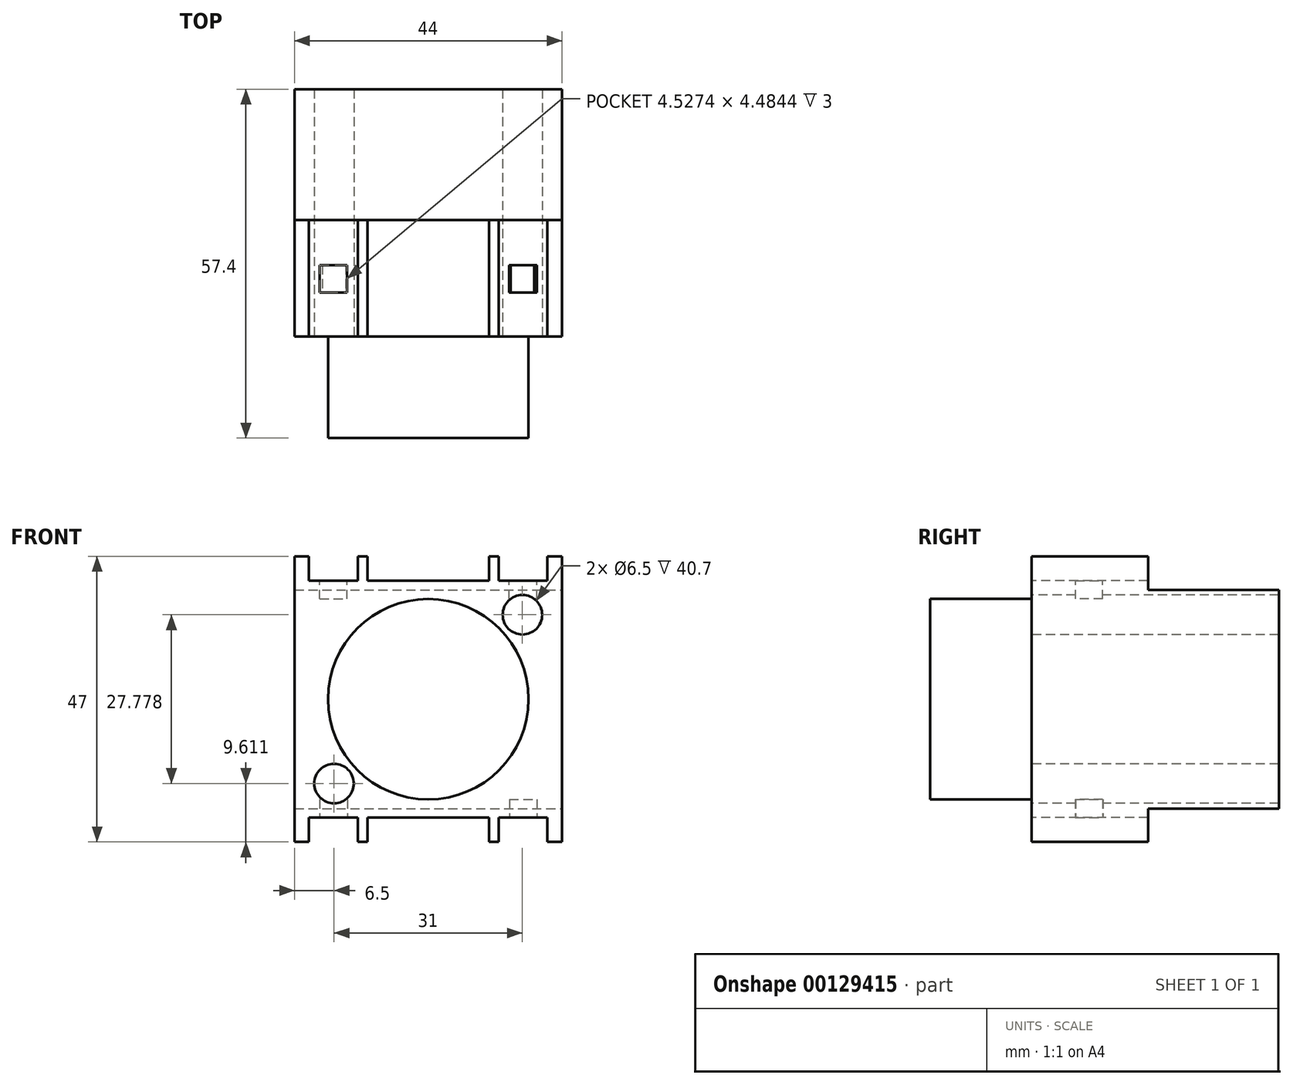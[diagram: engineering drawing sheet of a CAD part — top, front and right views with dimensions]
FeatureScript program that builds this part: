
annotation { "Feature Type Name" : "Feature", "Feature Type Description" : "" }
export const myFeature = defineFeature(function(context is Context, id is Id, definition is map)
    precondition{}
    {
        {
            var Q0;
            Q0=qCreatedBy(makeId("Front.planeOp"),FACE);
            var sketch = newSketch(context, id + "F0", { "sketchPlane" : qUnion([Q0])});
            skLineSegment(sketch, "E0.bottom", {"start": v(22, -23.5) * mm, "end": v(19.62, -23.5) * mm});
            skLineSegment(sketch, "E0.left", {"start": v(22, -23.5) * mm, "end": v(22, 23.5) * mm});
            skLineSegment(sketch, "E0.right", {"start": v(-22, -23.5) * mm, "end": v(-22, 23.5) * mm});
            skPoint(sketch, "E0.middle", {"position": v(0, 0) * mm});
            skLineSegment(sketch, "E1", {"start": v(-22, 23.5) * mm, "end": v(-22, 19.5) * mm});
            skLineSegment(sketch, "E2", {"start": v(-19.62, 19.5) * mm, "end": v(-11.58, 19.5) * mm});
            skLineSegment(sketch, "E3.MirrorCS", {"start": v(-19.62, -19.5) * mm, "end": v(-11.58, -19.5) * mm});
            skLineSegment(sketch, "E4.left", {"start": v(2.3, 19.5) * mm, "end": v(2.3, 23.5) * mm});
            skLineSegment(sketch, "E4.right", {"start": v(-2.3, 19.5) * mm, "end": v(-2.3, 23.5) * mm});
            skLineSegment(sketch, "E5", {"start": v(-2.3, 19.5) * mm, "end": v(-9.98, 19.5) * mm});
            skLineSegment(sketch, "E6.left", {"start": v(-9.98, 19.5) * mm, "end": v(-9.98, 23.5) * mm});
            skLineSegment(sketch, "E6.right", {"start": v(-11.58, 19.5) * mm, "end": v(-11.58, 23.5) * mm});
            skLineSegment(sketch, "E7.top", {"start": v(-22, 23.5) * mm, "end": v(-19.62, 23.5) * mm});
            skLineSegment(sketch, "E7.left", {"start": v(-22, 19.5) * mm, "end": v(-22, 23.5) * mm});
            skLineSegment(sketch, "E7.right", {"start": v(-19.62, 19.5) * mm, "end": v(-19.62, 23.5) * mm});
            skLineSegment(sketch, "E8.MirrorCS", {"start": v(22, 23.5) * mm, "end": v(19.62, 23.5) * mm});
            skLineSegment(sketch, "E9.MirrorCS", {"start": v(22, 23.5) * mm, "end": v(22, 19.5) * mm});
            skLineSegment(sketch, "E10.MirrorCS", {"start": v(22, 19.5) * mm, "end": v(22, 23.5) * mm});
            skLineSegment(sketch, "E11.MirrorCS", {"start": v(9.98, 19.5) * mm, "end": v(9.98, 23.5) * mm});
            skLineSegment(sketch, "E12.MirrorCS", {"start": v(11.58, 19.5) * mm, "end": v(11.58, 23.5) * mm});
            skLineSegment(sketch, "E13.MirrorCS", {"start": v(19.62, 19.5) * mm, "end": v(19.62, 23.5) * mm});
            skLineSegment(sketch, "E14.MirrorCS", {"start": v(-22, -23.5) * mm, "end": v(-19.62, -23.5) * mm});
            skLineSegment(sketch, "E15.MirrorCS", {"start": v(9.98, -19.5) * mm, "end": v(9.98, -23.5) * mm});
            skLineSegment(sketch, "E16.MirrorCS", {"start": v(-9.98, -19.5) * mm, "end": v(-9.98, -23.5) * mm});
            skLineSegment(sketch, "E17.MirrorCS", {"start": v(-2.3, -19.5) * mm, "end": v(-2.3, -23.5) * mm});
            skLineSegment(sketch, "E18.MirrorCS", {"start": v(-11.58, -19.5) * mm, "end": v(-11.58, -23.5) * mm});
            skLineSegment(sketch, "E19.MirrorCS", {"start": v(11.58, -19.5) * mm, "end": v(11.58, -23.5) * mm});
            skLineSegment(sketch, "E20.MirrorCS", {"start": v(22, -23.5) * mm, "end": v(22, -19.5) * mm});
            skLineSegment(sketch, "E21.MirrorCS", {"start": v(-22, -23.5) * mm, "end": v(-22, -19.5) * mm});
            skPoint(sketch, "E22.MirrorP", {"position": v(10.78, -23.5) * mm});
            skLineSegment(sketch, "E23.MirrorCS", {"start": v(-22, -19.5) * mm, "end": v(-22, -23.5) * mm});
            skLineSegment(sketch, "E24.MirrorCS", {"start": v(22, -19.5) * mm, "end": v(22, -23.5) * mm});
            skLineSegment(sketch, "E25.MirrorCS", {"start": v(19.62, -19.5) * mm, "end": v(19.62, -23.5) * mm});
            skPoint(sketch, "E26.MirrorP", {"position": v(0, -23.5) * mm});
            skLineSegment(sketch, "E27.MirrorCS", {"start": v(2.3, -19.5) * mm, "end": v(2.3, -23.5) * mm});
            skLineSegment(sketch, "E28.MirrorCS", {"start": v(-19.62, -19.5) * mm, "end": v(-19.62, -23.5) * mm});
            skPoint(sketch, "E29.MirrorP", {"position": v(-10.78, -23.5) * mm});
            skLineSegment(sketch, "E30.trimOffspring", {"start": v(-19.62, -23.5) * mm, "end": v(-22, -23.5) * mm});
            skLineSegment(sketch, "E31.trimOffspring", {"start": v(-9.98, -23.5) * mm, "end": v(-11.58, -23.5) * mm});
            skLineSegment(sketch, "E32.trimOffspring", {"start": v(2.3, -23.5) * mm, "end": v(-2.3, -23.5) * mm});
            skLineSegment(sketch, "E33.trimOffspring", {"start": v(11.58, -23.5) * mm, "end": v(9.98, -23.5) * mm});
            skLineSegment(sketch, "E34.trimOffspring", {"start": v(11.58, 23.5) * mm, "end": v(9.98, 23.5) * mm});
            skLineSegment(sketch, "E35.trimOffspring", {"start": v(-9.98, 23.5) * mm, "end": v(-11.58, 23.5) * mm});
            skLineSegment(sketch, "E36.trimOffspring", {"start": v(11.58, 19.5) * mm, "end": v(19.62, 19.5) * mm});
            skLineSegment(sketch, "E37.trimOffspring", {"start": v(2.3, 19.5) * mm, "end": v(9.98, 19.5) * mm});
            skLineSegment(sketch, "E38", {"start": v(-2.3, 23.5) * mm, "end": v(2.3, 23.5) * mm});
            skLineSegment(sketch, "E39.trimOffspring", {"start": v(-9.98, 19.5) * mm, "end": v(-2.3, 19.5) * mm});
            skLineSegment(sketch, "E40.trimOffspring", {"start": v(-19.62, 23.5) * mm, "end": v(-22, 23.5) * mm});
            skLineSegment(sketch, "E41.trimOffspring", {"start": v(11.58, -19.5) * mm, "end": v(19.62, -19.5) * mm});
            skLineSegment(sketch, "E42.trimOffspring", {"start": v(2.3, -19.5) * mm, "end": v(9.98, -19.5) * mm});
            skLineSegment(sketch, "E43.trimOffspring", {"start": v(-9.98, -19.5) * mm, "end": v(-2.3, -19.5) * mm});
            skCircle(sketch, "E44", {"center": v(0, 0) * mm, "radius": 16.5 * mm});
            skLineSegment(sketch, "E45", {"start": v(-22, 23.5) * mm, "end": v(-22, 13.9) * mm});
            skLineSegment(sketch, "E46", {"start": v(-22, 13.9) * mm, "end": v(-15.5, 13.89) * mm});
            skCircle(sketch, "E47", {"center": v(-15.5, 13.89) * mm, "radius": 3.25 * mm});
            skCircle(sketch, "E48.MirrorC", {"center": v(15.5, 13.89) * mm, "radius": 3.25 * mm});
            skCircle(sketch, "E49.MirrorC", {"center": v(15.5, -13.89) * mm, "radius": 3.25 * mm});
            skCircle(sketch, "E50.MirrorC", {"center": v(-15.5, -13.89) * mm, "radius": 3.25 * mm});
            skSolve(sketch);
        }
        {
            var Q0;
            Q0=makeQuery(id+"F0.imprint","IMPRINT",FACE,{"disambiguationData":[TD([[makeQuery(id+"F0.imprint","IMPRINT",EDGE,{"derivedFrom":sQuery(id+"F0.wireOp",EDGE,"E0.left")}),1.0]])]});
            var Q1;
            Q1=makeQuery(id+"F0.imprint","IMPRINT",FACE,{"disambiguationData":[TD([[makeQuery(id+"F0.imprint","IMPRINT",EDGE,{"derivedFrom":sQuery(id+"F0.wireOp",EDGE,"E47")}),1.0]])]});
            var Q2;
            Q2=makeQuery(id+"F0.imprint","IMPRINT",FACE,{"disambiguationData":[TD([[makeQuery(id+"F0.imprint","IMPRINT",EDGE,{"derivedFrom":sQuery(id+"F0.wireOp",EDGE,"E48.MirrorC")}),-1.0]])]});
            var Q3;
            Q3=makeQuery(id+"F0.imprint","IMPRINT",FACE,{"disambiguationData":[TD([[makeQuery(id+"F0.imprint","IMPRINT",EDGE,{"derivedFrom":sQuery(id+"F0.wireOp",EDGE,"E44")}),1.0]])]});
            var Q4;
            Q4=makeQuery(id+"F0.imprint","IMPRINT",FACE,{"disambiguationData":[TD([[makeQuery(id+"F0.imprint","IMPRINT",EDGE,{"derivedFrom":sQuery(id+"F0.wireOp",EDGE,"E50.MirrorC")}),-1.0]])]});
            var Q5;
            Q5=makeQuery(id+"F0.imprint","IMPRINT",FACE,{"disambiguationData":[TD([[makeQuery(id+"F0.imprint","IMPRINT",EDGE,{"derivedFrom":sQuery(id+"F0.wireOp",EDGE,"E49.MirrorC")}),1.0]])]});
            extrude(context, id + "F1", {"entities" : qUnion([Q0, Q1, Q2, Q3, Q4, Q5]), "oppositeDirection" : true, "depth" : 22.2 * mm});
        }
        {
            var Q0;
            Q0=makeQuery(id+"F1.opExtrude","SWEPT_FACE",FACE,{"disambiguationData":[OSD([sQuery(id+"F0.wireOp",EDGE,"E38")])]});
            var sketch = newSketch(context, id + "F2", { "sketchPlane" : qUnion([Q0])});
            skLineSegment(sketch, "E51.bottom", {"start": v(-2.3, 22.2) * mm, "end": v(2.3, 22.2) * mm});
            skLineSegment(sketch, "E51.top", {"start": v(-2.3, 1.7) * mm, "end": v(2.3, 1.7) * mm});
            skLineSegment(sketch, "E51.left", {"start": v(-2.3, 22.2) * mm, "end": v(-2.3, 1.7) * mm});
            skLineSegment(sketch, "E51.right", {"start": v(2.3, 22.2) * mm, "end": v(2.3, 1.7) * mm});
            skSolve(sketch);
        }
        {
            var Q0;
            Q0=makeQuery(id+"F2.imprint","IMPRINT",FACE,{"disambiguationData":[TD([[makeQuery(id+"F2.imprint","IMPRINT",EDGE,{"derivedFrom":sQuery(id+"F2.wireOp",EDGE,"E51.bottom")}),-1.0]])]});
            extrude(context, id + "F3", {"entities" : qUnion([Q0]), "operationType" : NewBodyOperationType.REMOVE, "oppositeDirection" : true, "depth" : 4 * mm});
        }
        {
            var Q0;
            Q0=makeQuery(id+"F1.opExtrude","SWEPT_FACE",FACE,{"disambiguationData":[OSD([sQuery(id+"F0.wireOp",EDGE,"E32.trimOffspring")])]});
            var sketch = newSketch(context, id + "F4", { "sketchPlane" : qUnion([Q0])});
            skLineSegment(sketch, "E52.bottom", {"start": v(2.3, -22.2) * mm, "end": v(-2.3, -22.2) * mm});
            skLineSegment(sketch, "E52.top", {"start": v(2.3, -1.7) * mm, "end": v(-2.3, -1.7) * mm});
            skLineSegment(sketch, "E52.left", {"start": v(2.3, -22.2) * mm, "end": v(2.3, -1.7) * mm});
            skLineSegment(sketch, "E52.right", {"start": v(-2.3, -22.2) * mm, "end": v(-2.3, -1.7) * mm});
            skSolve(sketch);
        }
        {
            var Q0;
            Q0=makeQuery(id+"F4.imprint","IMPRINT",FACE,{"disambiguationData":[TD([[makeQuery(id+"F4.imprint","IMPRINT",EDGE,{"derivedFrom":sQuery(id+"F4.wireOp",EDGE,"E52.bottom")}),-1.0]])]});
            extrude(context, id + "F5", {"entities" : qUnion([Q0]), "operationType" : NewBodyOperationType.REMOVE, "oppositeDirection" : true, "depth" : 4 * mm});
        }
        {
            var Q0;
            Q0=makeQuery(id+"F0.imprint","IMPRINT",FACE,{"disambiguationData":[TD([[makeQuery(id+"F0.imprint","IMPRINT",EDGE,{"derivedFrom":sQuery(id+"F0.wireOp",EDGE,"E47")}),1.0]])]});
            var Q1;
            Q1=makeQuery(id+"F0.imprint","IMPRINT",FACE,{"disambiguationData":[TD([[makeQuery(id+"F0.imprint","IMPRINT",EDGE,{"derivedFrom":sQuery(id+"F0.wireOp",EDGE,"E48.MirrorC")}),-1.0]])]});
            var Q2;
            Q2=makeQuery(id+"F0.imprint","IMPRINT",FACE,{"disambiguationData":[TD([[makeQuery(id+"F0.imprint","IMPRINT",EDGE,{"derivedFrom":sQuery(id+"F0.wireOp",EDGE,"E49.MirrorC")}),1.0]])]});
            var Q3;
            Q3=makeQuery(id+"F0.imprint","IMPRINT",FACE,{"disambiguationData":[TD([[makeQuery(id+"F0.imprint","IMPRINT",EDGE,{"derivedFrom":sQuery(id+"F0.wireOp",EDGE,"E50.MirrorC")}),-1.0]])]});
            extrude(context, id + "F6", {"entities" : qUnion([Q0, Q1, Q2, Q3]), "operationType" : NewBodyOperationType.REMOVE, "oppositeDirection" : true, "depth" : 3 * mm});
        }
        {
            var Q0;
            Q0=makeQuery(id+"F0.imprint","IMPRINT",FACE,{"disambiguationData":[TD([[makeQuery(id+"F0.imprint","IMPRINT",EDGE,{"derivedFrom":sQuery(id+"F0.wireOp",EDGE,"E44")}),1.0]])]});
            extrude(context, id + "F7", {"entities" : qUnion([Q0]), "operationType" : NewBodyOperationType.ADD, "depth" : 13.7 * mm});
        }
        {
            var Q0;
            Q0=makeQuery(id+"F1.opExtrude","CAP_FACE",FACE,{"disambiguationData":[OSD([sQuery(id+"F0.wireOp",EDGE,"E0.left"),sQuery(id+"F0.wireOp",EDGE,"E0.right"),sQuery(id+"F0.wireOp",EDGE,"E2"),sQuery(id+"F0.wireOp",EDGE,"E3.MirrorCS"),sQuery(id+"F0.wireOp",EDGE,"E4.left"),sQuery(id+"F0.wireOp",EDGE,"E4.right"),sQuery(id+"F0.wireOp",EDGE,"E6.left"),sQuery(id+"F0.wireOp",EDGE,"E6.right"),sQuery(id+"F0.wireOp",EDGE,"E7.right"),sQuery(id+"F0.wireOp",EDGE,"E8.MirrorCS"),sQuery(id+"F0.wireOp",EDGE,"E10.MirrorCS"),sQuery(id+"F0.wireOp",EDGE,"E11.MirrorCS"),sQuery(id+"F0.wireOp",EDGE,"E12.MirrorCS"),sQuery(id+"F0.wireOp",EDGE,"E13.MirrorCS"),sQuery(id+"F0.wireOp",EDGE,"E15.MirrorCS"),sQuery(id+"F0.wireOp",EDGE,"E16.MirrorCS"),sQuery(id+"F0.wireOp",EDGE,"E17.MirrorCS"),sQuery(id+"F0.wireOp",EDGE,"E18.MirrorCS"),sQuery(id+"F0.wireOp",EDGE,"E19.MirrorCS"),sQuery(id+"F0.wireOp",EDGE,"E23.MirrorCS"),sQuery(id+"F0.wireOp",EDGE,"E24.MirrorCS"),sQuery(id+"F0.wireOp",EDGE,"E25.MirrorCS"),sQuery(id+"F0.wireOp",EDGE,"E27.MirrorCS"),sQuery(id+"F0.wireOp",EDGE,"E28.MirrorCS"),sQuery(id+"F0.wireOp",EDGE,"E0.bottom"),sQuery(id+"F0.wireOp",EDGE,"E31.trimOffspring"),sQuery(id+"F0.wireOp",EDGE,"E32.trimOffspring"),sQuery(id+"F0.wireOp",EDGE,"E33.trimOffspring"),sQuery(id+"F0.wireOp",EDGE,"E34.trimOffspring"),sQuery(id+"F0.wireOp",EDGE,"E35.trimOffspring"),sQuery(id+"F0.wireOp",EDGE,"E36.trimOffspring"),sQuery(id+"F0.wireOp",EDGE,"E37.trimOffspring"),sQuery(id+"F0.wireOp",EDGE,"E38"),sQuery(id+"F0.wireOp",EDGE,"E39.trimOffspring"),sQuery(id+"F0.wireOp",EDGE,"E40.trimOffspring"),sQuery(id+"F0.wireOp",EDGE,"E42.trimOffspring"),sQuery(id+"F0.wireOp",EDGE,"E41.trimOffspring"),sQuery(id+"F0.wireOp",EDGE,"E30.trimOffspring"),sQuery(id+"F0.wireOp",EDGE,"E43.trimOffspring"),sQuery(id+"F0.wireOp",EDGE,"E45")])],"isStart":false});
            var sketch = newSketch(context, id + "F8", { "sketchPlane" : qUnion([Q0])});
            skPoint(sketch, "E53", {"position": v(0, 0) * mm});
            skLineSegment(sketch, "E54.bottom", {"start": v(22, 18) * mm, "end": v(-22, 18) * mm});
            skLineSegment(sketch, "E54.top", {"start": v(22, -18) * mm, "end": v(-22, -18) * mm});
            skLineSegment(sketch, "E54.left", {"start": v(22, 18) * mm, "end": v(22, -18) * mm});
            skLineSegment(sketch, "E54.right", {"start": v(-22, 18) * mm, "end": v(-22, -18) * mm});
            skSolve(sketch);
        }
        {
            var Q0;
            Q0=makeQuery(id+"F8.imprint","IMPRINT",FACE,{"disambiguationData":[TD([[makeQuery(id+"F8.imprint","IMPRINT",EDGE,{"derivedFrom":sQuery(id+"F8.wireOp",EDGE,"E54.bottom")}),1.0]])]});
            extrude(context, id + "F9", {"entities" : qUnion([Q0]), "operationType" : NewBodyOperationType.ADD, "depth" : 21.5 * mm});
        }
        {
            var Q0;
            Q0=makeQuery(id+"F1.opExtrude","SWEPT_FACE",FACE,{"disambiguationData":[OSD([sQuery(id+"F0.wireOp",EDGE,"E36.trimOffspring")])]});
            var sketch = newSketch(context, id + "F10", { "sketchPlane" : qUnion([Q0])});
            skLineSegment(sketch, "E55", {"start": v(15.6, 0) * mm, "end": v(15.6, 12.5) * mm});
            skLineSegment(sketch, "E56.bottom", {"start": v(17.86, 10.26) * mm, "end": v(13.34, 10.26) * mm});
            skLineSegment(sketch, "E56.top", {"start": v(17.86, 14.74) * mm, "end": v(13.34, 14.74) * mm});
            skLineSegment(sketch, "E56.left", {"start": v(17.86, 10.26) * mm, "end": v(17.86, 14.74) * mm});
            skLineSegment(sketch, "E56.right", {"start": v(13.34, 10.26) * mm, "end": v(13.34, 14.74) * mm});
            skPoint(sketch, "E56.middle", {"position": v(15.6, 12.5) * mm});
            skLineSegment(sketch, "E57.MirrorCS", {"start": v(-13.34, 10.26) * mm, "end": v(-13.34, 14.74) * mm});
            skLineSegment(sketch, "E58.MirrorCS", {"start": v(-17.86, 10.26) * mm, "end": v(-17.86, 14.74) * mm});
            skLineSegment(sketch, "E59.MirrorCS", {"start": v(-17.86, 14.74) * mm, "end": v(-13.34, 14.74) * mm});
            skPoint(sketch, "E60.MirrorP", {"position": v(-15.6, 12.5) * mm});
            skLineSegment(sketch, "E61.MirrorCS", {"start": v(-17.86, 10.26) * mm, "end": v(-13.34, 10.26) * mm});
            skSolve(sketch);
        }
        {
            var Q0;
            Q0=makeQuery(id+"F1.opExtrude","SWEPT_FACE",FACE,{"disambiguationData":[OSD([sQuery(id+"F0.wireOp",EDGE,"E3.MirrorCS")])]});
            var sketch = newSketch(context, id + "F11", { "sketchPlane" : qUnion([Q0])});
            skLineSegment(sketch, "E62.bottom", {"start": v(-13.32, -10.26) * mm, "end": v(-17.84, -10.26) * mm});
            skLineSegment(sketch, "E62.top", {"start": v(-13.32, -14.74) * mm, "end": v(-17.84, -14.74) * mm});
            skLineSegment(sketch, "E62.left", {"start": v(-13.32, -10.26) * mm, "end": v(-13.32, -14.74) * mm});
            skLineSegment(sketch, "E62.right", {"start": v(-17.84, -10.26) * mm, "end": v(-17.84, -14.74) * mm});
            skPoint(sketch, "E62.middle", {"position": v(-15.58, -12.5) * mm});
            skLineSegment(sketch, "E63.bottom", {"start": v(13.37, -10.2) * mm, "end": v(17.88, -10.2) * mm});
            skLineSegment(sketch, "E63.top", {"start": v(13.37, -14.8) * mm, "end": v(17.88, -14.8) * mm});
            skLineSegment(sketch, "E63.left", {"start": v(13.37, -10.2) * mm, "end": v(13.37, -14.8) * mm});
            skLineSegment(sketch, "E63.right", {"start": v(17.88, -10.2) * mm, "end": v(17.88, -14.8) * mm});
            skPoint(sketch, "E63.middle", {"position": v(15.63, -12.5) * mm});
            skPoint(sketch, "E63.middle.positionSnap0", {"position": v(-13.32, -12.5) * mm});
            skPoint(sketch, "E63.centerSnap0", {"position": v(-13.32, -12.5) * mm});
            skSolve(sketch);
        }
        {
            var Q0;
            Q0=makeQuery(id+"F10.imprint","IMPRINT",FACE,{"disambiguationData":[TD([[makeQuery(id+"F10.imprint","IMPRINT",EDGE,{"derivedFrom":sQuery(id+"F10.wireOp",EDGE,"E57.MirrorCS")}),1.0]])]});
            var Q1;
            Q1=makeQuery(id+"F10.imprint","IMPRINT",FACE,{"disambiguationData":[TD([[makeQuery(id+"F10.imprint","IMPRINT",EDGE,{"derivedFrom":sQuery(id+"F10.wireOp",EDGE,"E56.top")}),1.0]])]});
            extrude(context, id + "F12", {"entities" : qUnion([Q0, Q1]), "operationType" : NewBodyOperationType.REMOVE, "oppositeDirection" : true, "depth" : 3 * mm});
        }
        {
            var Q0;
            Q0=makeQuery(id+"F11.imprint","IMPRINT",FACE,{"disambiguationData":[TD([[makeQuery(id+"F11.imprint","IMPRINT",EDGE,{"derivedFrom":sQuery(id+"F11.wireOp",EDGE,"E63.bottom")}),-1.0]])]});
            var Q1;
            Q1=makeQuery(id+"F11.imprint","IMPRINT",FACE,{"disambiguationData":[TD([[makeQuery(id+"F11.imprint","IMPRINT",EDGE,{"derivedFrom":sQuery(id+"F11.wireOp",EDGE,"E62.bottom")}),1.0]])]});
            extrude(context, id + "F13", {"entities" : qUnion([Q0, Q1]), "operationType" : NewBodyOperationType.REMOVE, "oppositeDirection" : true, "depth" : 3 * mm});
        }
    });
